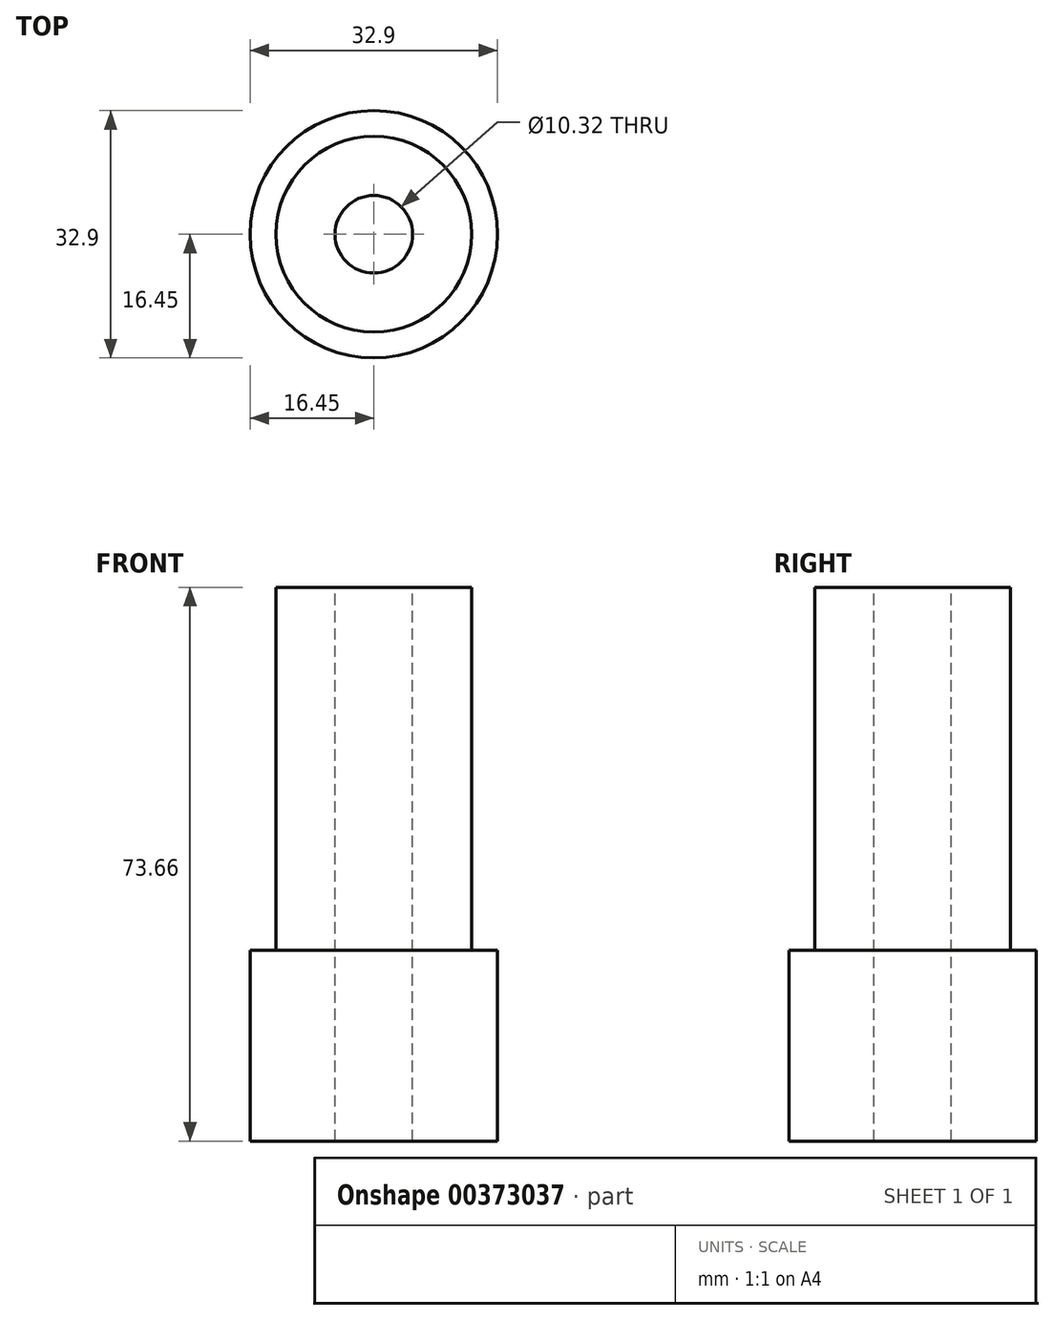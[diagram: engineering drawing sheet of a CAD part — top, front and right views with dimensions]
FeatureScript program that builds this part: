
annotation { "Feature Type Name" : "Feature", "Feature Type Description" : "" }
export const myFeature = defineFeature(function(context is Context, id is Id, definition is map)
    precondition{}
    {
        {
            var Q0;
            Q0=qCreatedBy(makeId("Top.planeOp"),FACE);
            var sketch = newSketch(context, id + "F0", { "sketchPlane" : qUnion([Q0])});
            skCircle(sketch, "E0", {"center": v(0, 0) * mm, "radius": 16.45 * mm});
            skSolve(sketch);
        }
        {
            var Q0;
            Q0 = qSketchRegion(id + "F0", true);
            extrude(context, id + "F1", {"entities" : qUnion([Q0]), "depth" : 25.4 * mm});
        }
        {
            var Q0;
            Q0=makeQuery(id+"F1.opExtrude","CAP_FACE",FACE,{"disambiguationData":[OSD([sQuery(id+"F0.wireOp",EDGE,"E0")])],"isStart":false});
            var sketch = newSketch(context, id + "F2", { "sketchPlane" : qUnion([Q0])});
            skCircle(sketch, "E1", {"center": v(0, 0) * mm, "radius": 13.02 * mm});
            skSolve(sketch);
        }
        {
            var Q0;
            Q0=makeQuery(id+"F2.imprint","IMPRINT",FACE,{"disambiguationData":[TD([[makeQuery(id+"F2.imprint","IMPRINT",EDGE,{"derivedFrom":sQuery(id+"F2.wireOp",EDGE,"E1")}),1.0]])]});
            extrude(context, id + "F3", {"entities" : qUnion([Q0]), "operationType" : NewBodyOperationType.ADD, "depth" : 48.26 * mm});
        }
        {
            var Q0;
            Q0=makeQuery(id+"F3.opExtrude","CAP_FACE",FACE,{"disambiguationData":[OSD([sQuery(id+"F2.wireOp",EDGE,"E1")])],"isStart":false});
            var sketch = newSketch(context, id + "F4", { "sketchPlane" : qUnion([Q0])});
            skPoint(sketch, "E2", {"position": v(0, 0) * mm});
            skSolve(sketch);
        }
        {
            var Q0;
            Q0=sQuery(id+"F4.wireOp",VERTEX,"E2");
            var Q1;
            Q1=makeQuery(id+"F1.opExtrude","SWEPT_BODY",BODY,{"disambiguationData":[OSD([sQuery(id+"F0.wireOp",EDGE,"E0")])]});
            hole(context, id + "F5", {"style" : HoleStyle.SIMPLE, "endStyle" : HoleEndStyle.THROUGH, "holeDiameter" : 10.32 * mm, "isTappedThrough" : true, "tappedDepth" : 12.7 * mm, "tapClearance" : 3, "startFromSketch" : true, "locations" : qUnion([Q0]), "scope" : qUnion([Q1])});
        }
    });
